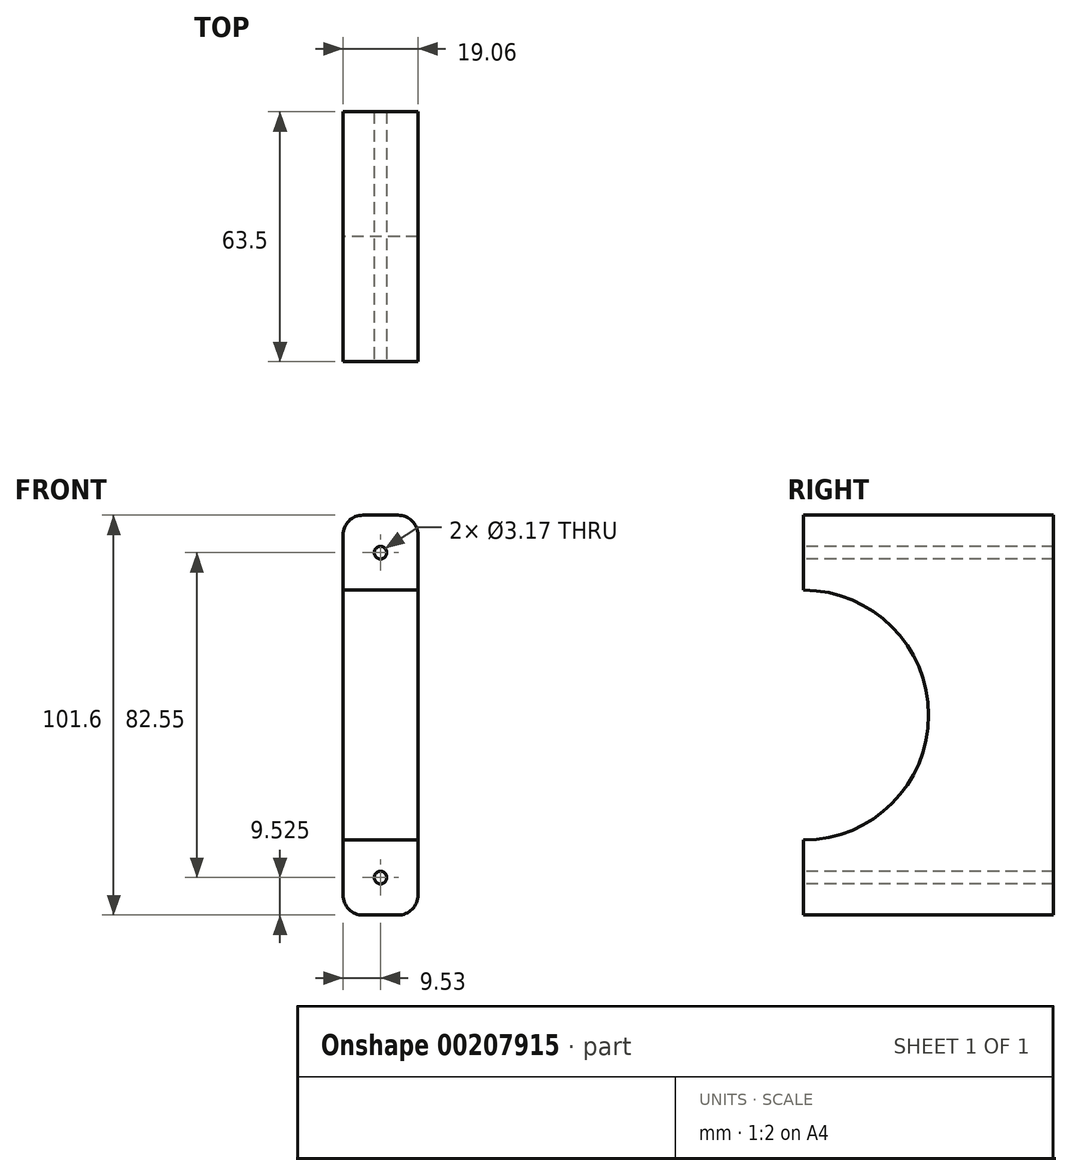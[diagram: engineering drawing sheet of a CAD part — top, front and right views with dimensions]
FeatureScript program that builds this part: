
annotation { "Feature Type Name" : "Feature", "Feature Type Description" : "" }
export const myFeature = defineFeature(function(context is Context, id is Id, definition is map)
    precondition{}
    {
        {
            var Q0;
            Q0=qCreatedBy(makeId("Front.planeOp"),FACE);
            var sketch = newSketch(context, id + "F0", { "sketchPlane" : qUnion([Q0])});
            skLineSegment(sketch, "E0.bottom", {"start": v(9.53, 50.8) * mm, "end": v(-9.52, 50.8) * mm});
            skLineSegment(sketch, "E0.top", {"start": v(9.52, -50.8) * mm, "end": v(-9.53, -50.8) * mm});
            skLineSegment(sketch, "E0.left", {"start": v(9.53, 50.8) * mm, "end": v(9.52, -50.8) * mm});
            skLineSegment(sketch, "E0.right", {"start": v(-9.52, 50.8) * mm, "end": v(-9.53, -50.8) * mm});
            skPoint(sketch, "E0.middle", {"position": v(0, 0) * mm});
            skSolve(sketch);
        }
        {
            var Q0;
            Q0 = qSketchRegion(id + "F0", true);
            extrude(context, id + "F1", {"entities" : qUnion([Q0]), "depth" : 63.5 * mm});
        }
        {
            var Q0;
            Q0=makeQuery(id+"F1.opExtrude","SWEPT_FACE",FACE,{"disambiguationData":[OSD([sQuery(id+"F0.wireOp",EDGE,"E0.right")])]});
            cPlane(context, id + "F2", {"entities" : qUnion([Q0]), "cplaneType" : CPlaneType.OFFSET, "offset" : 0 * mm, "width" : 152.4 * mm, "height" : 152.4 * mm});
        }
        {
            var Q0;
            Q0=qCreatedBy(id+"F2.planeOp",FACE);
            var sketch = newSketch(context, id + "F3", { "sketchPlane" : qUnion([Q0])});
            skPoint(sketch, "E1.0", {"position": v(63.5, 0) * mm});
            skCircle(sketch, "E2", {"center": v(63.5, 0) * mm, "radius": 31.75 * mm});
            skSolve(sketch);
        }
        {
            var Q0;
            Q0 = qSketchRegion(id + "F3", true);
            extrude(context, id + "F4", {"entities" : qUnion([Q0]), "operationType" : NewBodyOperationType.REMOVE, "oppositeDirection" : true, "depth" : 19.05 * mm});
        }
        {
            var Q0;
            {var subQ0=sQuery(id+"F0.wireOp",EDGE,"E0.bottom");var subQ1=sQuery(id+"F0.wireOp",EDGE,"E0.left");var subQ2=sQuery(id+"F0.wireOp",EDGE,"E0.right");Q0=makeQuery(id+"F4.boolean.opBoolean","SPLIT",FACE,{"disambiguationData":[TD([makeQuery(id+"F1.opExtrude","SWEPT_FACE",FACE,{"disambiguationData":[OSD([subQ0])]})])],"derivedFrom":makeQuery(id+"F1.opExtrude","CAP_FACE",FACE,{"disambiguationData":[OSD([subQ0,sQuery(id+"F0.wireOp",EDGE,"E0.top"),subQ1,subQ2])],"isStart":false})});}
            cPlane(context, id + "F5", {"entities" : qUnion([Q0]), "cplaneType" : CPlaneType.OFFSET, "offset" : 0 * mm, "width" : 152.4 * mm, "height" : 152.4 * mm});
        }
        {
            var Q0;
            Q0=qCreatedBy(id+"F5.planeOp",FACE);
            var sketch = newSketch(context, id + "F6", { "sketchPlane" : qUnion([Q0])});
            skPoint(sketch, "E3.0", {"position": v(9.53, 41.28) * mm});
            skPoint(sketch, "E4.0", {"position": v(-9.52, 41.28) * mm});
            skPoint(sketch, "E5.0", {"position": v(0, 50.8) * mm});
            skPoint(sketch, "E6.0", {"position": v(0, 31.75) * mm});
            skLineSegment(sketch, "E7", {"start": v(9.53, 41.28) * mm, "end": v(-9.52, 41.28) * mm, "construction": true});
            skCircle(sketch, "E8", {"center": v(0, 41.28) * mm, "radius": 1.59 * mm});
            skCircle(sketch, "E9.MirrorC", {"center": v(0, -41.28) * mm, "radius": 1.59 * mm});
            skSolve(sketch);
        }
        {
            var Q0;
            Q0 = qSketchRegion(id + "F6", true);
            extrude(context, id + "F7", {"entities" : qUnion([Q0]), "operationType" : NewBodyOperationType.REMOVE, "oppositeDirection" : true, "depth" : 63.5 * mm});
        }
        {
            var Q0;
            Q0=makeQuery(id+"F1.opExtrude","SWEPT_EDGE",EDGE,{"disambiguationData":[OSD([sQuery(id+"F0.wireOp",EDGE,"E0.bottom"),sQuery(id+"F0.wireOp",EDGE,"E0.right")])]});
            var Q1;
            Q1=makeQuery(id+"F1.opExtrude","SWEPT_EDGE",EDGE,{"disambiguationData":[OSD([sQuery(id+"F0.wireOp",EDGE,"E0.top"),sQuery(id+"F0.wireOp",EDGE,"E0.right")])]});
            var Q2;
            Q2=makeQuery(id+"F1.opExtrude","SWEPT_EDGE",EDGE,{"disambiguationData":[OSD([sQuery(id+"F0.wireOp",EDGE,"E0.top"),sQuery(id+"F0.wireOp",EDGE,"E0.left")])]});
            var Q3;
            Q3=makeQuery(id+"F1.opExtrude","SWEPT_EDGE",EDGE,{"disambiguationData":[OSD([sQuery(id+"F0.wireOp",EDGE,"E0.bottom"),sQuery(id+"F0.wireOp",EDGE,"E0.left")])]});
            fillet(context, id + "F8", {"entities" : qUnion([Q0, Q1, Q2, Q3]), "radius" : 5.08 * mm, "tangentPropagation" : true, "allowEdgeOverflow" : false});
        }
    });
